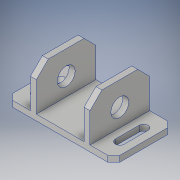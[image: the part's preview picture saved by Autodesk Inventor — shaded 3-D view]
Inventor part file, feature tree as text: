
AUTODESK INVENTOR PART (.ipt)
format: ipt  version: 2019 (Build 230136000, 136)  size: 168,448 bytes
history: native  units: in
note: dims shown in document units (in); Inventor stores cm internally (conversion verified against a paired STEP export)
features: extrude x4, sketch x4, chamfer x2, plane x1, mirror x1
ambient origin geometry x8: Origin, YZ Plane, XZ Plane, XY Plane, X Axis, Y Axis, Z Axis, Center Point
bodies: Solid1 (feature_tree)
feature tree (12):
  extrude  "Extrusion1"  Depth=5.0in
  chamfer  "Chamfer1"  Distance=0.5in
  extrude  "Extrusion2"  Depth=2.0in
  chamfer  "Chamfer2"  Distance=2.0in
  extrude  "Extrusion3"  Depth=0.5in
  extrude  "Extrusion5"  Depth=3.5in TaperAngle=0.0deg
  plane  "Work Plane1"
  mirror  "Mirror1"
  sketch  "Sketch1"  dims[d0=9.0in d1=5.0in d2=0.5in d3=0.0in]
  sketch  "Sketch2"  dims[d4=0.5in d5=0.125in d6=45.0deg d7=2.0in]
  sketch  "Sketch3"  dims[d8=5.0in]
  sketch  "Sketch6"  dims[d9=0.5in d10=2.0in d11=0.5in d12=3.5in d13=0.0in d14=1.0in d15=0.125in d16=45.0deg d17=2.0in d18=1.5in d19=3.0in d20=0.0in d31=0.75in d32=0.75in d33=1.0in d34=0.0in]
